# Revit family: Deca_Chuveiro com Tubo de Parede_Balance_1963.C.CT
name_source: partatom
category: Plumbing Fixtures
revit_build: Autodesk Revit Architecture 2012 (Build: 20110916_2132(x64)
units: mm (PartAtom-declared; Revit-internal decimal feet)

## types (1)
- 1363.C.CT
    Acompanha o Produto = Não Aplicável
    Aprovado por = Contino/quattroD
    Atendimento ao Cliente = 0800-011-7073
    Chuveiro = Deca CR10 Cromado Metal
    Consumo = Jato linear (7 l/min) , nebulizador (3,7 l/min)
    Criador por = Contino/quattroD
    Código = 1963.C.CT
    Default Elevation = 2100 mm
    Description = Chuveiro
    Descrição = Chuveiro
    Detalhes = Deca CZ87 Cinza real Plástico
    Diâmetro Ponto de Agua = 15 mm  [stored 0.0492126 ft]
    Fabricante = Deca
    Flow Pressure = 0.00 psi
    HWFU = 0
    Informações Complementares = Tubo parede
    Linha = Balance
    Louça/Metais = Metais
    Manufacturer = Deca
    Material = Metal
    Model = 1963.C.CT
    Norma = NBR 15206
    Peso Liquido (Kg) = 0.655
    Pressão = 10 a 40 mca
    Produto = Chuveiro tubo parede Balance 5 Jatos
    Raio Ponto de Agua = 8 mm  [stored 0.0262467 ft]
    Segmento = Médio
    URL = www.deca.com.br
    Vendido Separadamente = Não Aplicável

note: [stored X ft] marks values corroborated as IEEE doubles in the binary element streams (Revit-internal decimal feet)

## geometry (parser evidence)
native form markers: Blend x4, Sweep x1
no freeform markers — native parametric forms only
